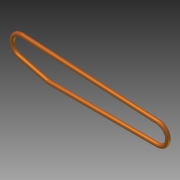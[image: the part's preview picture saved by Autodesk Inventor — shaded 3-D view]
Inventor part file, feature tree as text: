
AUTODESK INVENTOR PART (.ipt)
format: ipt  version: 2012 (Build 160160000, 160)  size: 96,256 bytes
history: native  units: in
note: dims shown in document units (in); Inventor stores cm internally (conversion verified against a paired STEP export)
features: sketch x2, sweep x1
ambient origin geometry x8: Origin, YZ Plane, XZ Plane, XY Plane, X Axis, Y Axis, Z Axis, Center Point
bodies: Solid1 (feature_tree)
feature tree (3):
  sweep  "Sweep1"
  sketch  "Sketch1"  dims[d0=6.75in d1=0.625in]
  sketch  "Sketch2"  dims[d2=1.804in d3=8.511in d4=0.625in d5=0.625in d6=0.625in d7=0.25in d8=0.0in]
